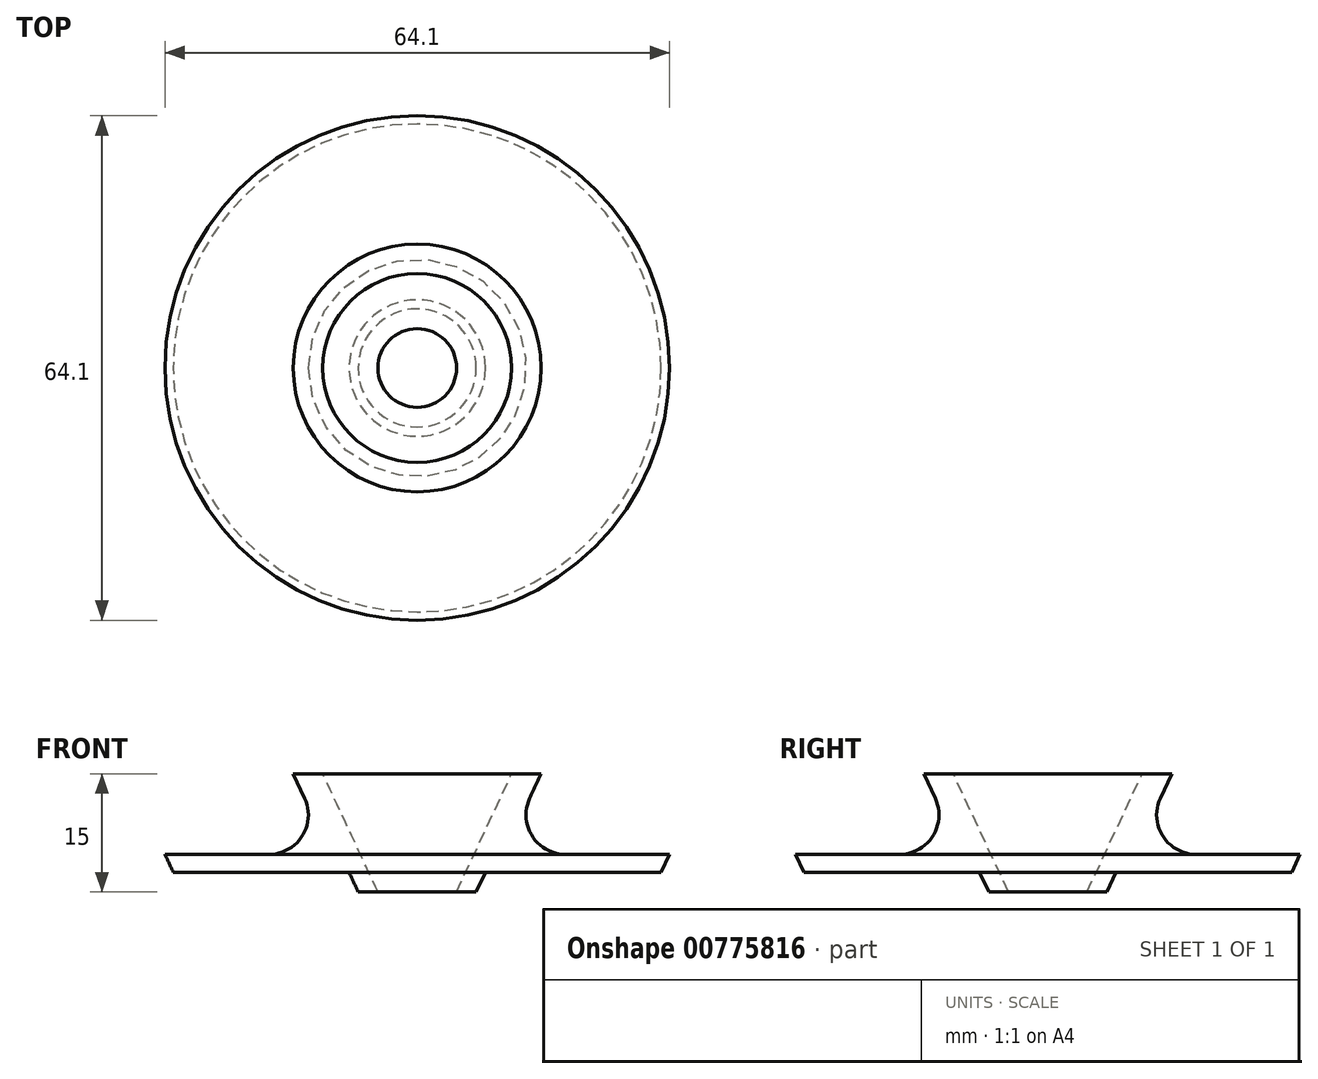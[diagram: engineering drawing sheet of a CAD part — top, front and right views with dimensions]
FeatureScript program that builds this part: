
annotation { "Feature Type Name" : "Feature", "Feature Type Description" : "" }
export const myFeature = defineFeature(function(context is Context, id is Id, definition is map)
    precondition{}
    {
        {
            var Q0;
            Q0=qCreatedBy(makeId("Front.planeOp"),FACE);
            var sketch = newSketch(context, id + "F0", { "sketchPlane" : qUnion([Q0])});
            skLineSegment(sketch, "E0", {"start": v(-5, 0) * mm, "end": v(-12, 15) * mm});
            skLineSegment(sketch, "E1", {"start": v(-12, 15) * mm, "end": v(-15.74, 15) * mm});
            skLineSegment(sketch, "E2", {"start": v(-15.74, 15) * mm, "end": v(-10.97, 4.77) * mm});
            skLineSegment(sketch, "E3", {"start": v(-10.97, 4.77) * mm, "end": v(-32.05, 4.77) * mm});
            skLineSegment(sketch, "E4", {"start": v(-32.05, 4.77) * mm, "end": v(-31, 2.5) * mm});
            skLineSegment(sketch, "E5", {"start": v(-31, 2.5) * mm, "end": v(-8.67, 2.5) * mm});
            skLineSegment(sketch, "E6", {"start": v(-8.67, 2.5) * mm, "end": v(-7.5, 0) * mm});
            skLineSegment(sketch, "E7", {"start": v(-7.5, 0) * mm, "end": v(-5, 0) * mm});
            skSolve(sketch);
        }
        {
            var Q0;
            Q0=qCreatedBy(makeId("Front.planeOp"),FACE);
            var sketch = newSketch(context, id + "F1", { "sketchPlane" : qUnion([Q0])});
            skLineSegment(sketch, "E8", {"start": v(0, 0) * mm, "end": v(0, 25.46) * mm});
            skSolve(sketch);
        }
        {
            var Q0;
            Q0=makeQuery(id+"F0.imprint","IMPRINT",FACE,{"disambiguationData":[TD([[makeQuery(id+"F0.imprint","IMPRINT",EDGE,{"derivedFrom":sQuery(id+"F0.wireOp",EDGE,"E0")}),1.0]])]});
            var Q1;
            Q1=sQuery(id+"F1.wireOp",EDGE,"E8");
            revolve(context, id + "F2", {"surfaceOperationType" : NewSurfaceOperationType.NEW, "entities" : qUnion([Q0]), "axis" : qUnion([Q1]), "revolveType" : RevolveType.FULL});
        }
        {
            var Q0;
            Q0=makeQuery(id+"F2.opRevolve","SWEPT_EDGE",EDGE,{"disambiguationData":[OSD([sQuery(id+"F0.wireOp",EDGE,"E2"),sQuery(id+"F0.wireOp",EDGE,"E3")])]});
            fillet(context, id + "F3", {"entities" : qUnion([Q0]), "radius" : 5 * mm, "tangentPropagation" : true, "allowEdgeOverflow" : false});
        }
    });
